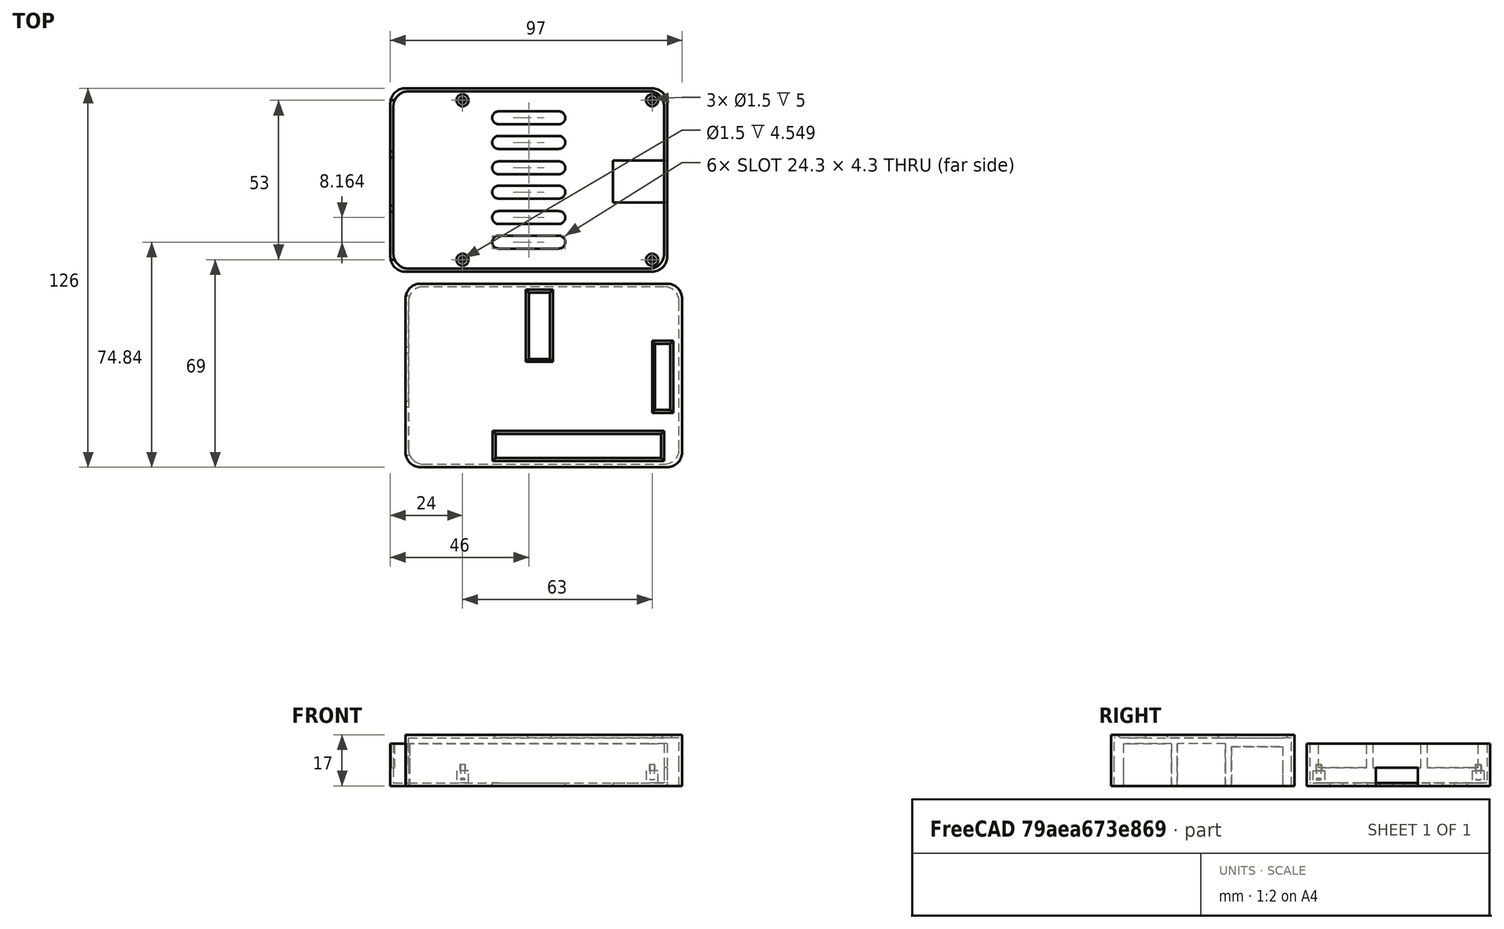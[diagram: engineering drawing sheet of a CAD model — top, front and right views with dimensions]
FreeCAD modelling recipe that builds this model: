
FCSTD DOCUMENT  (FreeCAD 0.18R16146 (Git))
Label: rasp
License: All rights reserved
LicenseURL: http://en.wikipedia.org/wiki/All_rights_reserved
objects: Sketcher::SketchObject×15, PartDesign::Pocket×10, PartDesign::Pad×6, PartDesign::Hole×4, PartDesign::Chamfer×3, PartDesign::Body×2, App::Part×2, Mesh::Feature×2
note: 60 computed .brp shape members not serialized (recipe doc carries the construction recipe); baked Part::Feature solids carry a one-line shape summary decoded from their .brp

FEATURE [Sketcher::SketchObject] Sketch
  MapMode = 5
  Support = -> [XY_Plane001]
  sketch-geometry (8):
    g0: LineSegment StartX=-41 StartY=30.5 StartZ=0 EndX=41 EndY=30.5 EndZ=0
    g1: LineSegment StartX=46 StartY=25.5 StartZ=0 EndX=46 EndY=-25.5 EndZ=0
    g2: LineSegment StartX=41 StartY=-30.5 StartZ=0 EndX=-41 EndY=-30.5 EndZ=0
    g3: LineSegment StartX=-46 StartY=-25.5 StartZ=0 EndX=-46 EndY=25.5 EndZ=0
    g4: ArcOfCircle CenterX=-41 CenterY=25.5 CenterZ=0 NormalX=0 NormalY=0 NormalZ=1 AngleXU=0 Radius=5 StartAngle=1.5708 EndAngle=3.14159
    g5: ArcOfCircle CenterX=-41 CenterY=-25.5 CenterZ=0 NormalX=0 NormalY=0 NormalZ=1 AngleXU=0 Radius=5 StartAngle=3.14159 EndAngle=4.71239
    g6: ArcOfCircle CenterX=41 CenterY=25.5 CenterZ=0 NormalX=0 NormalY=0 NormalZ=1 AngleXU=0 Radius=5 StartAngle=0 EndAngle=1.5708
    g7: ArcOfCircle CenterX=41 CenterY=-25.5 CenterZ=0 NormalX=0 NormalY=0 NormalZ=1 AngleXU=0 Radius=5 StartAngle=4.71239 EndAngle=6.28319
  constraints (21):
    c: Horizontal(g0)
    c: Horizontal(g2)
    c: Vertical(g1)
    c: Vertical(g3)
    c: Tangent(g0,g4) = 1.5708
    c: Tangent(g3,g4) = 1.5708
    c: Tangent(g2,g5) = 1.5708
    c: Tangent(g3,g5) = 1.5708
    c: Tangent(g0,g6) = 1.5708
    c: Tangent(g1,g6) = 1.5708
    c: Tangent(g1,g7) = 1.5708
    c: Tangent(g2,g7) = 1.5708
    c: Equal(g0,g2)
    c: Equal(g3,g1)
    c: Equal(g3,g1)
    c: Equal(g6,g4)
    c: Equal(g4,g5)
    c: DistanceX(g3,g1) = 92
    c: DistanceY(g2,g0) = 61
    c: Diameter(g4) = 10
    c: Symmetric(g6,g5,g-1)
FEATURE [PartDesign::Pad] Pad
  Length = 17
  Length2 = 100
  Profile = -> Sketch
  Type = 0
FEATURE [Sketcher::SketchObject] Sketch001
  ExternalGeometry = -> [Pad]
  MapMode = 5
  Placement = pos=(0,0,17) rot=(0,0,1;0rad)
  Support = -> [Pad]
  sketch-geometry (4):
    g0: LineSegment StartX=-16 StartY=-19.5 StartZ=0 EndX=39 EndY=-19.5 EndZ=0
    g1: LineSegment StartX=39 StartY=-19.5 StartZ=0 EndX=39 EndY=-27.5 EndZ=0
    g2: LineSegment StartX=39 StartY=-27.5 StartZ=0 EndX=-16 EndY=-27.5 EndZ=0
    g3: LineSegment StartX=-16 StartY=-27.5 StartZ=0 EndX=-16 EndY=-19.5 EndZ=0
  constraints (12):
    c: Coincident(g0,g1)
    c: Coincident(g1,g2)
    c: Coincident(g2,g3)
    c: Coincident(g3,g0)
    c: Horizontal(g0)
    c: Horizontal(g2)
    c: Vertical(g1)
    c: Vertical(g3)
    c: DistanceX(g0,g0) = 55
    c: DistanceY(g3,g3) = 8
    c: DistanceY(g-3,g1) = 3
    c: DistanceX(g0,g-5) = 7
FEATURE [PartDesign::Pocket] Pocket
  BaseFeature = -> Pad
  Length = 5
  Length2 = 100
  Profile = -> Sketch001
  Type = 1
FEATURE [PartDesign::Chamfer] Chamfer
  Base = -> Pocket [Edge27,Edge28,Edge25,Edge26]
  BaseFeature = -> Pocket
  Size = 1
FEATURE [Sketcher::SketchObject] Sketch002
  ExternalGeometry = -> [Chamfer]
  MapMode = 5
  Placement = pos=(0,0,17) rot=(0,0,1;0rad)
  Support = -> [Chamfer]
  sketch-geometry (4):
    g0: LineSegment StartX=-5 StartY=27.5 StartZ=0 EndX=2 EndY=27.5 EndZ=0
    g1: LineSegment StartX=2 StartY=27.5 StartZ=0 EndX=2 EndY=5.5 EndZ=0
    g2: LineSegment StartX=2 StartY=5.5 StartZ=0 EndX=-5 EndY=5.5 EndZ=0
    g3: LineSegment StartX=-5 StartY=5.5 StartZ=0 EndX=-5 EndY=27.5 EndZ=0
  constraints (12):
    c: Coincident(g0,g1)
    c: Coincident(g1,g2)
    c: Coincident(g2,g3)
    c: Coincident(g3,g0)
    c: Horizontal(g0)
    c: Horizontal(g2)
    c: Vertical(g1)
    c: Vertical(g3)
    c: DistanceX(g0,g-3) = 44
    c: DistanceX(g-4,g0) = 41
    c: DistanceY(g1,g0) = 22
    c: DistanceY(g0,g-5) = 3
FEATURE [PartDesign::Pocket] Pocket001
  BaseFeature = -> Chamfer
  Length = 5
  Length2 = 100
  Profile = -> Sketch002
  Type = 1
FEATURE [PartDesign::Chamfer] Chamfer001
  Base = -> Pocket001 [Edge9,Edge10,Edge11,Edge12]
  BaseFeature = -> Pocket001
  Size = 1
FEATURE [Sketcher::SketchObject] Sketch003
  ExternalGeometry = -> [Chamfer001]
  MapMode = 5
  Placement = pos=(0,0,17) rot=(0,0,1;0rad)
  Support = -> [Chamfer001]
  sketch-geometry (4):
    g0: LineSegment StartX=37 StartY=10.5 StartZ=0 EndX=42 EndY=10.5 EndZ=0
    g1: LineSegment StartX=42 StartY=10.5 StartZ=0 EndX=42 EndY=-11.5 EndZ=0
    g2: LineSegment StartX=42 StartY=-11.5 StartZ=0 EndX=37 EndY=-11.5 EndZ=0
    g3: LineSegment StartX=37 StartY=-11.5 StartZ=0 EndX=37 EndY=10.5 EndZ=0
  constraints (12):
    c: Coincident(g0,g1)
    c: Coincident(g1,g2)
    c: Coincident(g2,g3)
    c: Coincident(g3,g0)
    c: Horizontal(g0)
    c: Horizontal(g2)
    c: Vertical(g1)
    c: Vertical(g3)
    c: DistanceX(g1,g-3) = 4
    c: DistanceY(g0,g-4) = 20
    c: DistanceY(g2,g0) = 22
    c: DistanceX(g0,g0) = 5
FEATURE [PartDesign::Pocket] Pocket002
  BaseFeature = -> Chamfer001
  Length = 5
  Length2 = 100
  Profile = -> Sketch003
  Type = 1
FEATURE [PartDesign::Chamfer] Chamfer002
  Base = -> Pocket002 [Edge20,Edge19,Edge17,Edge18]
  BaseFeature = -> Pocket002
  Size = 1
FEATURE [Sketcher::SketchObject] Sketch004
  ExternalGeometry = -> [Sketch]
  MapMode = 5
  Placement = pos=(0,0,0) rot=(1,0,0;3.14159rad)
  Support = -> [Chamfer002]
  sketch-geometry (8):
    g0: LineSegment StartX=-40 StartY=29.5 StartZ=0 EndX=40 EndY=29.5 EndZ=0
    g1: LineSegment StartX=45 StartY=24.5 StartZ=0 EndX=45 EndY=-24.5 EndZ=0
    g2: LineSegment StartX=40 StartY=-29.5 StartZ=0 EndX=-40 EndY=-29.5 EndZ=0
    g3: LineSegment StartX=-45 StartY=-24.5 StartZ=0 EndX=-45 EndY=24.5 EndZ=0
    g4: ArcOfCircle CenterX=40 CenterY=24.5 CenterZ=0 NormalX=0 NormalY=0 NormalZ=1 AngleXU=0 Radius=5 StartAngle=1e-16 EndAngle=1.5708
    g5: ArcOfCircle CenterX=-40 CenterY=24.5 CenterZ=0 NormalX=0 NormalY=0 NormalZ=1 AngleXU=0 Radius=5 StartAngle=1.5708 EndAngle=3.14159
    g6: ArcOfCircle CenterX=-40 CenterY=-24.5 CenterZ=0 NormalX=0 NormalY=0 NormalZ=1 AngleXU=0 Radius=5 StartAngle=3.14159 EndAngle=4.71239
    g7: ArcOfCircle CenterX=40 CenterY=-24.5 CenterZ=0 NormalX=0 NormalY=0 NormalZ=1 AngleXU=0 Radius=5 StartAngle=4.71239 EndAngle=6.28319
  constraints (20):
    c: Horizontal(g0)
    c: Horizontal(g2)
    c: Vertical(g1)
    c: Vertical(g3)
    c: Tangent(g0,g4) = 1.5708
    c: Tangent(g1,g4) = 1.5708
    c: Tangent(g0,g5) = 1.5708
    c: Tangent(g3,g5) = 1.5708
    c: Tangent(g2,g6) = 1.5708
    c: Tangent(g3,g6) = 1.5708
    c: Tangent(g1,g7) = 1.5708
    c: Tangent(g2,g7) = 1.5708
    c: DistanceX(g1,g-3) = 1
    c: DistanceY(g0,g-4) = 1
    c: DistanceX(g-6,g3) = 1
    c: DistanceY(g-5,g2) = 1
    c: Diameter(g5) = 10
    c: Equal(g5,g4)
    c: Equal(g5,g7)
    c: Equal(g7,g6)
FEATURE [PartDesign::Pocket] Pocket003
  BaseFeature = -> Chamfer002
  Length = 7
  Length2 = 100
  Profile = -> Sketch004
  Type = 0
FEATURE [PartDesign::Pocket] Pocket004
  BaseFeature = -> Pocket003
  Length = 16
  Length2 = 100
  Profile = -> Sketch004
  Type = 0
FEATURE [Sketcher::SketchObject] Sketch005
  ExternalGeometry = -> [Pocket004]
  MapMode = 5
  Placement = pos=(-46,0,0) rot=(0.57735,-0.57735,-0.57735;2.0944rad)
  Support = -> [Pocket004]
  sketch-geometry (12):
    g0: LineSegment StartX=-26.5 StartY=13 StartZ=0 EndX=-9.5 EndY=13 EndZ=0
    g1: LineSegment StartX=-9.5 StartY=13 StartZ=0 EndX=-9.5 EndY=0 EndZ=0
    g2: LineSegment StartX=-9.5 StartY=0 StartZ=0 EndX=-26.5 EndY=0 EndZ=0
    g3: LineSegment StartX=-26.5 StartY=0 StartZ=0 EndX=-26.5 EndY=13 EndZ=0
    g4: LineSegment StartX=-7.5 StartY=14 StartZ=0 EndX=8.5 EndY=14 EndZ=0
    g5: LineSegment StartX=8.5 StartY=14 StartZ=0 EndX=8.5 EndY=0 EndZ=0
    g6: LineSegment StartX=8.5 StartY=0 StartZ=0 EndX=-7.5 EndY=0 EndZ=0
    g7: LineSegment StartX=-7.5 StartY=0 StartZ=0 EndX=-7.5 EndY=14 EndZ=0
    g8: LineSegment StartX=10.5 StartY=14 StartZ=0 EndX=26.5 EndY=14 EndZ=0
    g9: LineSegment StartX=26.5 StartY=14 StartZ=0 EndX=26.5 EndY=0 EndZ=0
    g10: LineSegment StartX=26.5 StartY=0 StartZ=0 EndX=10.5 EndY=0 EndZ=0
    g11: LineSegment StartX=10.5 StartY=0 StartZ=0 EndX=10.5 EndY=14 EndZ=0
  constraints (36):
    c: Coincident(g0,g1)
    c: Coincident(g1,g2)
    c: Coincident(g2,g3)
    c: Coincident(g3,g0)
    c: Horizontal(g0)
    c: Horizontal(g2)
    c: Vertical(g1)
    c: Vertical(g3)
    c: PointOnObject(g2,g-1)
    c: DistanceY(g0,g-4) = 4
    c: DistanceX(g0,g0) = 17
    c: Coincident(g4,g5)
    c: Coincident(g5,g6)
    c: Coincident(g6,g7)
    c: Coincident(g7,g4)
    c: Horizontal(g4)
    c: Horizontal(g6)
    c: Vertical(g5)
    c: Vertical(g7)
    c: PointOnObject(g5,g-1)
    c: DistanceX(g0,g4) = 2
    c: DistanceY(g4,g-4) = 3
    c: DistanceX(g4,g4) = 16
    c: Coincident(g8,g9)
    c: Coincident(g9,g10)
    c: Coincident(g10,g11)
    c: Coincident(g11,g8)
    c: Horizontal(g8)
    c: Horizontal(g10)
    c: Vertical(g9)
    c: Vertical(g11)
    c: PointOnObject(g10,g-1)
    c: DistanceX(g5,g10) = 2
    c: Horizontal(g8,g4)
    c: DistanceX(g8,g8) = 16
    c: DistanceX(g-5,g2) = 4
FEATURE [PartDesign::Pocket] Pocket005
  BaseFeature = -> Pocket004
  Length = 5
  Length2 = 100
  Profile = -> Sketch005
  Type = 0
FEATURE [PartDesign::Body] Body
  Group = -> [Sketch,Pad,Sketch001,Pocket,Chamfer,Sketch002,Pocket001,Chamfer001,Sketch003,Pocket002,Chamfer002,Sketch004,Pocket003,Pocket004,Sketch005,Pocket005]
  Origin = -> Origin001
  Tip = -> Pocket005
FEATURE [App::Part] Part  label="TapaSuperior"
  Group = -> [Body]
  Origin = -> Origin
FEATURE [Sketcher::SketchObject] Sketch006
  MapMode = 5
  Support = -> [XY_Plane003]
  expr: Constraints[19] = Sketch.Constraints[19]
  expr: Constraints[18] = Sketch.Constraints[18]
  expr: Constraints[17] = Sketch.Constraints[17]
  sketch-geometry (8):
    g0: LineSegment StartX=-41 StartY=30.5 StartZ=0 EndX=41 EndY=30.5 EndZ=0
    g1: LineSegment StartX=46 StartY=25.5 StartZ=0 EndX=46 EndY=-25.5 EndZ=0
    g2: LineSegment StartX=41 StartY=-30.5 StartZ=0 EndX=-41 EndY=-30.5 EndZ=0
    g3: LineSegment StartX=-46 StartY=-25.5 StartZ=0 EndX=-46 EndY=25.5 EndZ=0
    g4: ArcOfCircle CenterX=-41 CenterY=25.5 CenterZ=0 NormalX=0 NormalY=0 NormalZ=1 AngleXU=0 Radius=5 StartAngle=1.5708 EndAngle=3.14159
    g5: ArcOfCircle CenterX=-41 CenterY=-25.5 CenterZ=0 NormalX=0 NormalY=0 NormalZ=1 AngleXU=0 Radius=5 StartAngle=3.14159 EndAngle=4.71239
    g6: ArcOfCircle CenterX=41 CenterY=25.5 CenterZ=0 NormalX=0 NormalY=0 NormalZ=1 AngleXU=0 Radius=5 StartAngle=0 EndAngle=1.5708
    g7: ArcOfCircle CenterX=41 CenterY=-25.5 CenterZ=0 NormalX=0 NormalY=0 NormalZ=1 AngleXU=0 Radius=5 StartAngle=4.71239 EndAngle=6.28319
  constraints (21):
    c: Horizontal(g0)
    c: Horizontal(g2)
    c: Vertical(g1)
    c: Vertical(g3)
    c: Tangent(g0,g4) = 1.5708
    c: Tangent(g3,g4) = 1.5708
    c: Tangent(g2,g5) = 1.5708
    c: Tangent(g3,g5) = 1.5708
    c: Tangent(g0,g6) = 1.5708
    c: Tangent(g1,g6) = 1.5708
    c: Tangent(g1,g7) = 1.5708
    c: Tangent(g2,g7) = 1.5708
    c: Equal(g0,g2)
    c: Equal(g3,g1)
    c: Equal(g3,g1)
    c: Equal(g6,g4)
    c: Equal(g4,g5)
    c: DistanceX(g3,g1) = 92
    c: DistanceY(g2,g0) = 61
    c: Diameter(g4) = 10
    c: Symmetric(g6,g5,g-1)
FEATURE [PartDesign::Pad] Pad001
  Length = 14
  Length2 = 100
  Profile = -> Sketch006
  Reversed = true
  Type = 0
FEATURE [Sketcher::SketchObject] Sketch007
  ExternalGeometry = -> [Pad001]
  MapMode = 5
  Support = -> [Pad001]
  sketch-geometry (8):
    g0: LineSegment StartX=-40 StartY=29.5 StartZ=0 EndX=40 EndY=29.5 EndZ=0
    g1: LineSegment StartX=45 StartY=24.5 StartZ=0 EndX=45 EndY=-24.5 EndZ=0
    g2: LineSegment StartX=40 StartY=-29.5 StartZ=0 EndX=-40 EndY=-29.5 EndZ=0
    g3: LineSegment StartX=-45 StartY=-24.5 StartZ=0 EndX=-45 EndY=24.5 EndZ=0
    g4: ArcOfCircle CenterX=40 CenterY=24.5 CenterZ=0 NormalX=0 NormalY=0 NormalZ=1 AngleXU=0 Radius=5 StartAngle=0 EndAngle=1.5708
    g5: ArcOfCircle CenterX=-40 CenterY=24.5 CenterZ=0 NormalX=0 NormalY=0 NormalZ=1 AngleXU=0 Radius=5 StartAngle=1.5708 EndAngle=3.14159
    g6: ArcOfCircle CenterX=-40 CenterY=-24.5 CenterZ=0 NormalX=0 NormalY=0 NormalZ=1 AngleXU=0 Radius=5 StartAngle=3.14159 EndAngle=4.71239
    g7: ArcOfCircle CenterX=40 CenterY=-24.5 CenterZ=0 NormalX=0 NormalY=0 NormalZ=1 AngleXU=0 Radius=5 StartAngle=4.71239 EndAngle=6.28319
  constraints (20):
    c: Horizontal(g0)
    c: Horizontal(g2)
    c: Vertical(g1)
    c: Vertical(g3)
    c: Tangent(g0,g4) = 1.5708
    c: Tangent(g1,g4) = 1.5708
    c: Tangent(g0,g5) = 1.5708
    c: Tangent(g3,g5) = 1.5708
    c: Tangent(g2,g6) = 1.5708
    c: Tangent(g3,g6) = 1.5708
    c: Tangent(g1,g7) = 1.5708
    c: Tangent(g2,g7) = 1.5708
    c: Diameter(g5) = 10
    c: Equal(g5,g6)
    c: Equal(g5,g4)
    c: Equal(g5,g7)
    c: DistanceX(g1,g-5) = 1
    c: DistanceY(g0,g-3) = 1
    c: DistanceX(g-4,g3) = 1
    c: DistanceY(g-6,g2) = 1
FEATURE [PartDesign::Pocket] Pocket006
  BaseFeature = -> Pad001
  Length = 13
  Length2 = 100
  Profile = -> Sketch007
  Type = 0
FEATURE [Sketcher::SketchObject] Sketch008
  ExternalGeometry = -> [Pocket006]
  MapMode = 5
  Placement = pos=(46,0,0) rot=(0.57735,0.57735,0.57735;2.0944rad)
  Support = -> [Pocket006]
  sketch-geometry (4):
    g0: LineSegment StartX=-7.5 StartY=-8 StartZ=0 EndX=6.5 EndY=-8 EndZ=0
    g1: LineSegment StartX=6.5 StartY=-8 StartZ=0 EndX=6.5 EndY=-14 EndZ=0
    g2: LineSegment StartX=6.5 StartY=-14 StartZ=0 EndX=-7.5 EndY=-14 EndZ=0
    g3: LineSegment StartX=-7.5 StartY=-14 StartZ=0 EndX=-7.5 EndY=-8 EndZ=0
  constraints (12):
    c: Coincident(g0,g1)
    c: Coincident(g1,g2)
    c: Coincident(g2,g3)
    c: Coincident(g3,g0)
    c: Horizontal(g0)
    c: Horizontal(g2)
    c: Vertical(g1)
    c: Vertical(g3)
    c: Horizontal(g1,g-3)
    c: DistanceX(g1,g-3) = 24
    c: DistanceX(g-4,g2) = 23
    c: DistanceY(g0,g-5) = 8
FEATURE [PartDesign::Pocket] Pocket007
  BaseFeature = -> Pocket006
  Length = 18
  Length2 = 100
  Profile = -> Sketch008
  Type = 0
FEATURE [Sketcher::SketchObject] Sketch009
  ExternalGeometry = -> [Pocket007]
  MapMode = 5
  Placement = pos=(-46,0,0) rot=(0.57735,-0.57735,-0.57735;2.0944rad)
  Support = -> [Pocket007]
  sketch-geometry (12):
    g0: LineSegment StartX=-26.5 StartY=0 StartZ=0 EndX=-9.5 EndY=0 EndZ=0
    g1: LineSegment StartX=-9.5 StartY=0 StartZ=0 EndX=-9.5 EndY=-8 EndZ=0
    g2: LineSegment StartX=-9.5 StartY=-8 StartZ=0 EndX=-26.5 EndY=-8 EndZ=0
    g3: LineSegment StartX=-26.5 StartY=-8 StartZ=0 EndX=-26.5 EndY=0 EndZ=0
    g4: LineSegment StartX=-7.5 StartY=0 StartZ=0 EndX=8.5 EndY=0 EndZ=0
    g5: LineSegment StartX=8.5 StartY=0 StartZ=0 EndX=8.5 EndY=-8 EndZ=0
    g6: LineSegment StartX=8.5 StartY=-8 StartZ=0 EndX=-7.5 EndY=-8 EndZ=0
    g7: LineSegment StartX=-7.5 StartY=-8 StartZ=0 EndX=-7.5 EndY=0 EndZ=0
    g8: LineSegment StartX=10.5 StartY=0 StartZ=0 EndX=26.5 EndY=0 EndZ=0
    g9: LineSegment StartX=26.5 StartY=0 StartZ=0 EndX=26.5 EndY=-8 EndZ=0
    g10: LineSegment StartX=26.5 StartY=-8 StartZ=0 EndX=10.5 EndY=-8 EndZ=0
    g11: LineSegment StartX=10.5 StartY=-8 StartZ=0 EndX=10.5 EndY=0 EndZ=0
  constraints (36):
    c: Coincident(g0,g1)
    c: Coincident(g1,g2)
    c: Coincident(g2,g3)
    c: Coincident(g3,g0)
    c: Horizontal(g0)
    c: Horizontal(g2)
    c: Vertical(g1)
    c: Vertical(g3)
    c: DistanceY(g-4,g1) = 6
    c: DistanceX(g-3,g2) = 4
    c: PointOnObject(g0,g-1)
    c: DistanceX(g0,g0) = 17
    c: Coincident(g4,g5)
    c: Coincident(g5,g6)
    c: Coincident(g6,g7)
    c: Coincident(g7,g4)
    c: Horizontal(g4)
    c: Horizontal(g6)
    c: Vertical(g5)
    c: Vertical(g7)
    c: Horizontal(g1,g6)
    c: PointOnObject(g4,g-1)
    c: DistanceX(g1,g6) = 2
    c: DistanceX(g6,g5) = 16
    c: Coincident(g8,g9)
    c: Coincident(g9,g10)
    c: Coincident(g10,g11)
    c: Coincident(g11,g8)
    c: Horizontal(g8)
    c: Horizontal(g10)
    c: Vertical(g9)
    c: Vertical(g11)
    c: Horizontal(g5,g10)
    c: DistanceX(g5,g10) = 2
    c: DistanceX(g10,g9) = 16
    c: PointOnObject(g8,g-1)
FEATURE [PartDesign::Pocket] Pocket008
  BaseFeature = -> Pocket007
  Length = 5
  Length2 = 100
  Profile = -> Sketch009
  Type = 0
FEATURE [Sketcher::SketchObject] Sketch010
  ExternalGeometry = -> [Pocket008]
  MapMode = 5
  Placement = pos=(0,0,-13) rot=(0,0,1;0rad)
  Support = -> [Pocket008]
  sketch-geometry (2):
    g0: Circle CenterX=-22 CenterY=26.5 CenterZ=0 NormalX=0 NormalY=0 NormalZ=1 AngleXU=0 Radius=2
    g1: Circle CenterX=-22 CenterY=-26.5 CenterZ=0 NormalX=0 NormalY=0 NormalZ=1 AngleXU=0 Radius=2
  constraints (6):
    c: Diameter(g0) = 4
    c: Equal(g0,g1)
    c: DistanceX(g-3,g0) = 23
    c: Vertical(g0,g1)
    c: DistanceY(g0,g-4) = 3
    c: DistanceY(g-5,g1) = 3
FEATURE [PartDesign::Pad] Pad002
  BaseFeature = -> Pocket008
  Length = 4
  Length2 = 100
  Profile = -> Sketch010
  Type = 0
FEATURE [Sketcher::SketchObject] Sketch011
  AttachmentOffset = pos=(0,0,-9) rot=(0,0,1;0rad)
  ExternalGeometry = -> [Pad002]
  MapMode = 5
  Placement = pos=(0,0,-9) rot=(0,0,1;0rad)
  Support = -> [XY_Plane003]
  sketch-geometry (2):
    g0: Circle CenterX=-22 CenterY=26.5 CenterZ=0 NormalX=0 NormalY=0 NormalZ=1 AngleXU=0 Radius=1
    g1: Circle CenterX=-22 CenterY=-26.5 CenterZ=0 NormalX=0 NormalY=0 NormalZ=1 AngleXU=0 Radius=1
  constraints (4):
    c: Coincident(g0,g-3)
    c: Diameter(g0) = 2
    c: Coincident(g1,g-4)
    c: Equal(g0,g1)
FEATURE [PartDesign::Pad] Pad003
  BaseFeature = -> Pad002
  Length = 2
  Length2 = 100
  Profile = -> Sketch011
  Type = 0
FEATURE [Sketcher::SketchObject] Sketch012
  ExternalGeometry = -> [Pad003]
  MapMode = 5
  Placement = pos=(0,0,-13) rot=(0,0,1;0rad)
  Support = -> [Pad003]
  sketch-geometry (2):
    g0: Circle CenterX=41 CenterY=26.5 CenterZ=0 NormalX=0 NormalY=0 NormalZ=1 AngleXU=0 Radius=2
    g1: Circle CenterX=41 CenterY=-26.5 CenterZ=0 NormalX=0 NormalY=0 NormalZ=1 AngleXU=0 Radius=2
  constraints (6):
    c: Equal(g0,g1)
    c: Diameter(g0) = 4
    c: Horizontal(g-4,g1)
    c: DistanceX(g0,g-5) = 4
    c: Vertical(g0,g1)
    c: Horizontal(g-8,g0)
FEATURE [PartDesign::Pad] Pad004
  BaseFeature = -> Pad003
  Length = 4
  Length2 = 100
  Profile = -> Sketch012
  Type = 0
FEATURE [Sketcher::SketchObject] Sketch013
  AttachmentOffset = pos=(0,0,-9) rot=(0,0,1;0rad)
  ExternalGeometry = -> [Pad004]
  MapMode = 5
  Placement = pos=(0,0,-9) rot=(0,0,1;0rad)
  Support = -> [XY_Plane003]
  sketch-geometry (2):
    g0: Circle CenterX=41 CenterY=26.5 CenterZ=0 NormalX=0 NormalY=0 NormalZ=1 AngleXU=0 Radius=1
    g1: Circle CenterX=41 CenterY=-26.5 CenterZ=0 NormalX=0 NormalY=0 NormalZ=1 AngleXU=0 Radius=1
  constraints (4):
    c: Coincident(g0,g-3)
    c: Coincident(g1,g-4)
    c: Equal(g0,g1)
    c: Diameter(g0) = 2
FEATURE [PartDesign::Pad] Pad005
  BaseFeature = -> Pad004
  Length = 2
  Length2 = 100
  Profile = -> Sketch013
  Type = 0
FEATURE [PartDesign::Hole] Hole
  BaseFeature = -> Pad005
  Depth = 5
  DepthType = 0
  Diameter = 1.5014
  DrillPoint = 0
  DrillPointAngle = 118
  HoleCutCountersinkAngle = 82
  HoleCutDepth = 0
  HoleCutDiameter = 0
  HoleCutType = 0
  ModelActualThread = false
  Profile = -> Pad005 [Face47]
  Tapered = false
  TaperedAngle = 90
  ThreadAngle = 60
  ThreadClass = 0
  ThreadCutOffInner = 0.0381917
  ThreadCutOffOuter = 0.0763834
  ThreadDirection = 1
  ThreadFit = 0
  ThreadPitch = 0.3528
  ThreadSize = 1
  ThreadType = 4
  Threaded = true
FEATURE [PartDesign::Hole] Hole001
  BaseFeature = -> Hole
  Depth = 5
  DepthType = 0
  Diameter = 1.5014
  DrillPoint = 0
  DrillPointAngle = 118
  HoleCutCountersinkAngle = 82
  HoleCutDepth = 0
  HoleCutDiameter = 0
  HoleCutType = 0
  ModelActualThread = false
  Profile = -> Hole [Face48]
  Tapered = false
  TaperedAngle = 90
  ThreadAngle = 60
  ThreadClass = 0
  ThreadCutOffInner = 0.0381917
  ThreadCutOffOuter = 0.0763834
  ThreadDirection = 1
  ThreadFit = 0
  ThreadPitch = 0.3528
  ThreadSize = 1
  ThreadType = 4
  Threaded = true
FEATURE [PartDesign::Hole] Hole002
  BaseFeature = -> Hole001
  Depth = 5
  DepthType = 0
  Diameter = 1.5014
  DrillPoint = 0
  DrillPointAngle = 118
  HoleCutCountersinkAngle = 82
  HoleCutDepth = 0
  HoleCutDiameter = 0
  HoleCutType = 0
  ModelActualThread = false
  Profile = -> Hole001 [Face50]
  Tapered = false
  TaperedAngle = 90
  ThreadAngle = 60
  ThreadClass = 0
  ThreadCutOffInner = 0.0381917
  ThreadCutOffOuter = 0.0763834
  ThreadDirection = 1
  ThreadFit = 0
  ThreadPitch = 0.3528
  ThreadSize = 1
  ThreadType = 4
  Threaded = true
FEATURE [PartDesign::Hole] Hole003
  BaseFeature = -> Hole002
  Depth = 5
  DepthType = 0
  Diameter = 1.5014
  DrillPoint = 1
  DrillPointAngle = 118
  HoleCutCountersinkAngle = 82
  HoleCutDepth = 0
  HoleCutDiameter = 0
  HoleCutType = 0
  ModelActualThread = false
  Profile = -> Hole002 [Face49]
  Tapered = false
  TaperedAngle = 90
  ThreadAngle = 60
  ThreadClass = 0
  ThreadCutOffInner = 0.0381917
  ThreadCutOffOuter = 0.0763834
  ThreadDirection = 1
  ThreadFit = 0
  ThreadPitch = 0.3528
  ThreadSize = 1
  ThreadType = 4
  Threaded = true
FEATURE [Sketcher::SketchObject] Sketch014
  MapMode = 5
  Placement = pos=(0,0,-13) rot=(0,0,1;0rad)
  Support = -> [Hole003]
  sketch-geometry (24):
    g0: ArcOfCircle CenterX=-10 CenterY=20.6601 CenterZ=0 NormalX=0 NormalY=0 NormalZ=1 AngleXU=0 Radius=2.15025 StartAngle=1.5708 EndAngle=4.71239
    g1: ArcOfCircle CenterX=10 CenterY=20.6601 CenterZ=0 NormalX=0 NormalY=0 NormalZ=1 AngleXU=0 Radius=2.15025 StartAngle=4.71239 EndAngle=7.85398
    g2: LineSegment StartX=-10 StartY=18.5099 StartZ=0 EndX=10 EndY=18.5099 EndZ=0
    g3: LineSegment StartX=-10 StartY=22.8104 StartZ=0 EndX=10 EndY=22.8104 EndZ=0
    g4: ArcOfCircle CenterX=-10 CenterY=12.496 CenterZ=0 NormalX=0 NormalY=0 NormalZ=1 AngleXU=0 Radius=2.15025 StartAngle=1.5708 EndAngle=4.71239
    g5: ArcOfCircle CenterX=10 CenterY=12.496 CenterZ=0 NormalX=0 NormalY=0 NormalZ=1 AngleXU=0 Radius=2.15025 StartAngle=4.71239 EndAngle=7.85398
    g6: LineSegment StartX=-10 StartY=10.3457 StartZ=0 EndX=10 EndY=10.3457 EndZ=0
    g7: LineSegment StartX=-10 StartY=14.6462 StartZ=0 EndX=10 EndY=14.6462 EndZ=0
    g8: ArcOfCircle CenterX=-10 CenterY=4.03503 CenterZ=0 NormalX=0 NormalY=0 NormalZ=1 AngleXU=0 Radius=2.15025 StartAngle=1.5708 EndAngle=4.71239
    g9: ArcOfCircle CenterX=10 CenterY=4.03503 CenterZ=0 NormalX=0 NormalY=0 NormalZ=1 AngleXU=0 Radius=2.15025 StartAngle=4.71239 EndAngle=7.85398
    g10: LineSegment StartX=-10 StartY=1.88478 StartZ=0 EndX=10 EndY=1.88478 EndZ=0
    g11: LineSegment StartX=-10 StartY=6.18528 StartZ=0 EndX=10 EndY=6.18528 EndZ=0
    g12: ArcOfCircle CenterX=10 CenterY=-20.6601 CenterZ=0 NormalX=0 NormalY=0 NormalZ=1 AngleXU=0 Radius=2.15025 StartAngle=4.71239 EndAngle=7.85398
    g13: ArcOfCircle CenterX=-10 CenterY=-20.6601 CenterZ=0 NormalX=0 NormalY=0 NormalZ=1 AngleXU=0 Radius=2.15025 StartAngle=1.5708 EndAngle=4.71239
    g14: LineSegment StartX=10 StartY=-18.5099 StartZ=0 EndX=-10 EndY=-18.5099 EndZ=0
    g15: LineSegment StartX=10 StartY=-22.8104 StartZ=0 EndX=-10 EndY=-22.8104 EndZ=0
    g16: ArcOfCircle CenterX=10 CenterY=-12.496 CenterZ=0 NormalX=0 NormalY=0 NormalZ=1 AngleXU=0 Radius=2.15025 StartAngle=4.71239 EndAngle=7.85398
    g17: ArcOfCircle CenterX=-10 CenterY=-12.496 CenterZ=0 NormalX=0 NormalY=0 NormalZ=1 AngleXU=0 Radius=2.15025 StartAngle=1.5708 EndAngle=4.71239
    g18: LineSegment StartX=10 StartY=-10.3457 StartZ=0 EndX=-10 EndY=-10.3457 EndZ=0
    g19: LineSegment StartX=10 StartY=-14.6462 StartZ=0 EndX=-10 EndY=-14.6462 EndZ=0
    g20: ArcOfCircle CenterX=10 CenterY=-4.03503 CenterZ=0 NormalX=0 NormalY=0 NormalZ=1 AngleXU=0 Radius=2.15025 StartAngle=4.71239 EndAngle=7.85398
    g21: ArcOfCircle CenterX=-10 CenterY=-4.03503 CenterZ=0 NormalX=0 NormalY=0 NormalZ=1 AngleXU=0 Radius=2.15025 StartAngle=1.5708 EndAngle=4.71239
    g22: LineSegment StartX=10 StartY=-1.88478 StartZ=0 EndX=-10 EndY=-1.88478 EndZ=0
    g23: LineSegment StartX=10 StartY=-6.18528 StartZ=0 EndX=-10 EndY=-6.18528 EndZ=0
  constraints (42):
    c: Tangent(g0,g3) = 1.5708
    c: Tangent(g0,g2) = -1.5708
    c: Tangent(g2,g1) = -1.5708
    c: Tangent(g3,g1) = 1.5708
    c: Horizontal(g2)
    c: Tangent(g4,g7) = 1.5708
    c: Tangent(g4,g6) = -1.5708
    c: Tangent(g6,g5) = -1.5708
    c: Tangent(g7,g5) = 1.5708
    c: Horizontal(g6)
    c: Tangent(g8,g11) = 1.5708
    c: Tangent(g8,g10) = -1.5708
    c: Tangent(g10,g9) = -1.5708
    c: Tangent(g11,g9) = 1.5708
    c: Horizontal(g10)
    c: Symmetric(g9,g8,g-2)
    c: Symmetric(g5,g4,g-2)
    c: Symmetric(g1,g0,g-2)
    c: DistanceX(g3,g3) = 20
    c: Equal(g3,g7)
    c: Equal(g7,g11)
    c: Equal(g1,g5)
    c: Equal(g1,g9)
    c: Tangent(g12,g15) = 1.5708
    c: Tangent(g12,g14) = -1.5708
    c: Tangent(g14,g13) = -1.5708
    c: Tangent(g15,g13) = 1.5708
    c: Horizontal(g14)
    c: Tangent(g16,g19) = 1.5708
    c: Tangent(g16,g18) = -1.5708
    c: Tangent(g18,g17) = -1.5708
    c: Tangent(g19,g17) = 1.5708
    c: Horizontal(g18)
    c: Tangent(g20,g23) = 1.5708
    c: Tangent(g20,g22) = -1.5708
    c: Tangent(g22,g21) = -1.5708
    c: Tangent(g23,g21) = 1.5708
    c: Horizontal(g22)
    c: Equal(g15,g19)
    c: Equal(g19,g23)
    c: Equal(g13,g17)
    c: Equal(g13,g21)
FEATURE [PartDesign::Pocket] Pocket009
  BaseFeature = -> Hole003
  Length = 5
  Length2 = 100
  Profile = -> Sketch014
  Type = 0
FEATURE [PartDesign::Body] Body001
  Group = -> [Sketch006,Pad001,Sketch007,Pocket006,Sketch008,Pocket007,Sketch009,Pocket008,Sketch010,Pad002,Sketch011,Pad003,Sketch012,Pad004,Sketch013,Pad005,Hole,Hole001,Hole002,Hole003,Sketch014,Pocket009]
  Origin = -> Origin003
  Placement = pos=(-5,65,14) rot=(0,0,1;0rad)
  Tip = -> Pocket009
FEATURE [App::Part] Part001  label="tapaInferior"
  Group = -> [Body001]
  Origin = -> Origin002
FEATURE [Mesh::Feature] Mesh  label="Pocket009 (Meshed)"
FEATURE [Mesh::Feature] Mesh001  label="Pocket005 (Meshed)"
